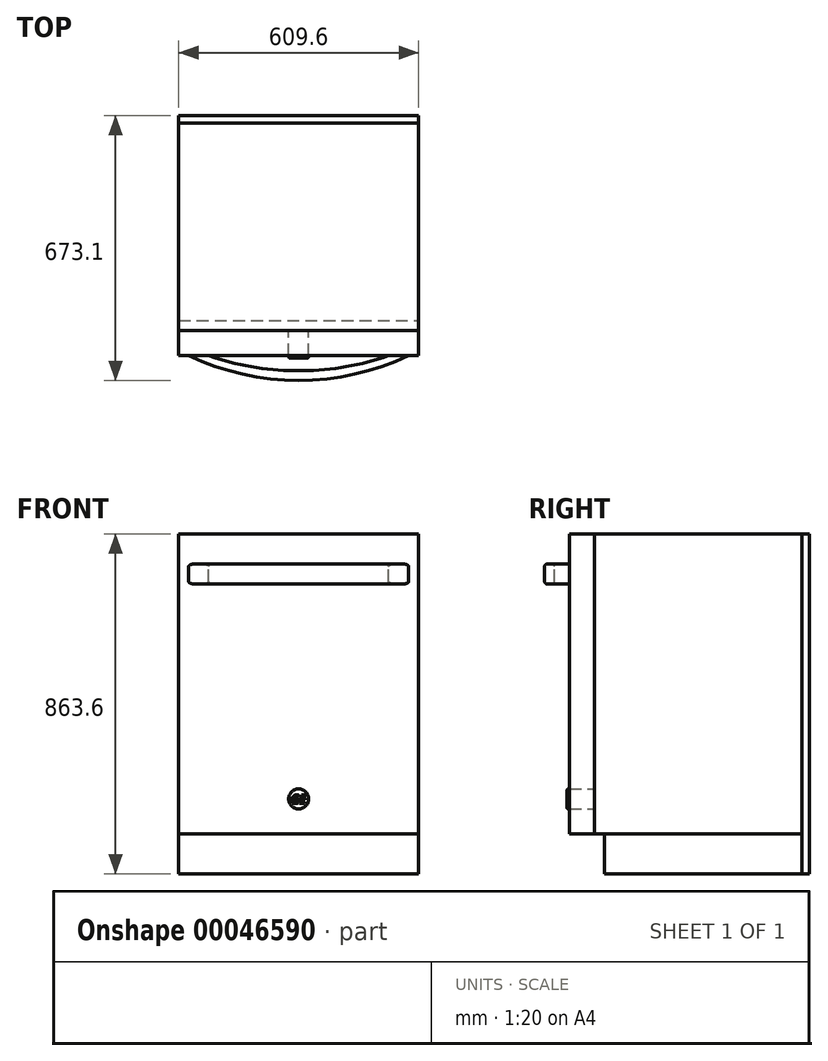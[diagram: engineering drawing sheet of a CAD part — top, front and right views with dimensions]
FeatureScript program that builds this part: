
annotation { "Feature Type Name" : "Feature", "Feature Type Description" : "" }
export const myFeature = defineFeature(function(context is Context, id is Id, definition is map)
    precondition{}
    {
        {
            var Q0;
            Q0=qCreatedBy(makeId("Front.planeOp"),FACE);
            var sketch = newSketch(context, id + "F0", { "sketchPlane" : qUnion([Q0])});
            skLineSegment(sketch, "E0.bottom", {"start": v(-304.8, 431.8) * mm, "end": v(304.8, 431.8) * mm});
            skLineSegment(sketch, "E0.top", {"start": v(-304.8, -431.8) * mm, "end": v(304.8, -431.8) * mm});
            skLineSegment(sketch, "E0.left", {"start": v(-304.8, 431.8) * mm, "end": v(-304.8, -431.8) * mm});
            skLineSegment(sketch, "E0.right", {"start": v(304.8, 431.8) * mm, "end": v(304.8, -431.8) * mm});
            skLineSegment(sketch, "E1", {"start": v(-304.8, 431.8) * mm, "end": v(304.8, -431.8) * mm, "construction": true});
            skLineSegment(sketch, "E2.bottom", {"start": v(-304.8, -330.2) * mm, "end": v(304.8, -330.2) * mm});
            skLineSegment(sketch, "E2.left", {"start": v(-304.8, -330.2) * mm, "end": v(-304.8, 431.8) * mm});
            skLineSegment(sketch, "E2.right", {"start": v(304.8, -330.2) * mm, "end": v(304.8, 431.8) * mm});
            skLineSegment(sketch, "E3", {"start": v(0, 0) * mm, "end": v(0, -330.2) * mm, "construction": true});
            skCircle(sketch, "E4", {"center": v(0, -241.3) * mm, "radius": 25.4 * mm});
            skLineSegment(sketch, "E5.bottom", {"start": v(-279.4, 355.6) * mm, "end": v(279.4, 355.6) * mm});
            skLineSegment(sketch, "E5.top", {"start": v(-279.4, 304.8) * mm, "end": v(279.4, 304.8) * mm});
            skLineSegment(sketch, "E5.left", {"start": v(-279.4, 355.6) * mm, "end": v(-279.4, 304.8) * mm});
            skLineSegment(sketch, "E5.right", {"start": v(279.4, 355.6) * mm, "end": v(279.4, 304.8) * mm});
            skLineSegment(sketch, "E6", {"start": v(0, 431.8) * mm, "end": v(0, 304.8) * mm, "construction": true});
            skSolve(sketch);
        }
        {
            var Q0;
            Q0=makeQuery(id+"F0.imprint","IMPRINT",FACE,{"disambiguationData":[TD([[makeQuery(id+"F0.imprint","IMPRINT",EDGE,{"derivedFrom":sQuery(id+"F0.wireOp",EDGE,"E2.bottom")}),1.0]])]});
            var Q1;
            Q1=makeQuery(id+"F0.imprint","IMPRINT",FACE,{"disambiguationData":[TD([[makeQuery(id+"F0.imprint","IMPRINT",EDGE,{"derivedFrom":sQuery(id+"F0.wireOp",EDGE,"E5.bottom")}),-1.0]])]});
            var Q2;
            Q2=makeQuery(id+"F0.imprint","IMPRINT",FACE,{"disambiguationData":[TD([[makeQuery(id+"F0.imprint","IMPRINT",EDGE,{"derivedFrom":sQuery(id+"F0.wireOp",EDGE,"E4")}),1.0]])]});
            var Q3;
            Q3=sQuery(id+"F0.wireOp",EDGE,"E2.right");
            var Q4;
            Q4=sQuery(id+"F0.wireOp",EDGE,"E0.bottom");
            var Q5;
            Q5=sQuery(id+"F0.wireOp",EDGE,"E2.left");
            var Q6;
            Q6=sQuery(id+"F0.wireOp",EDGE,"E2.bottom");
            extrude(context, id + "F1", {"entities" : qUnion([Q0, Q1, Q2]), "surfaceEntities" : qUnion([Q3, Q4, Q5, Q6]), "depth" : 63.5 * mm});
        }
        {
            var Q0;
            Q0=makeQuery(id+"F0.imprint","IMPRINT",FACE,{"disambiguationData":[TD([[makeQuery(id+"F0.imprint","IMPRINT",EDGE,{"derivedFrom":sQuery(id+"F0.wireOp",EDGE,"E0.top")}),1.0]])]});
            extrude(context, id + "F2", {"entities" : qUnion([Q0]), "oppositeDirection" : true, "depth" : 527.05 * mm});
        }
        {
            var Q0;
            Q0=makeQuery(id+"F0.imprint","IMPRINT",FACE,{"disambiguationData":[TD([[makeQuery(id+"F0.imprint","IMPRINT",EDGE,{"derivedFrom":sQuery(id+"F0.wireOp",EDGE,"E5.bottom")}),-1.0]])]});
            extrude(context, id + "F3", {"entities" : qUnion([Q0]), "operationType" : NewBodyOperationType.ADD, "depth" : 127 * mm});
        }
        {
            var Q0;
            Q0=makeQuery(id+"F3.opExtrude","SWEPT_FACE",FACE,{"disambiguationData":[OSD([sQuery(id+"F0.wireOp",EDGE,"E5.bottom")])]});
            var sketch = newSketch(context, id + "F4", { "sketchPlane" : qUnion([Q0])});
            skLineSegment(sketch, "E7.bottom", {"start": v(-228.6, -63.5) * mm, "end": v(228.6, -63.5) * mm});
            skLineSegment(sketch, "E7.top", {"start": v(-228.6, -101.6) * mm, "end": v(228.6, -101.6) * mm});
            skLineSegment(sketch, "E7.left", {"start": v(-228.6, -63.5) * mm, "end": v(-228.6, -101.6) * mm});
            skLineSegment(sketch, "E7.right", {"start": v(228.6, -63.5) * mm, "end": v(228.6, -101.6) * mm});
            skSolve(sketch);
        }
        {
            var Q0;
            Q0 = qSketchRegion(id + "F4", true);
            extrude(context, id + "F5", {"entities" : qUnion([Q0]), "operationType" : NewBodyOperationType.REMOVE, "endBound" : BoundingType.THROUGH_ALL, "oppositeDirection" : true, "depth" : 25.4 * mm});
        }
        {
            var Q0;
            Q0=makeQuery(id+"F5.boolean.opBoolean","COPY",EDGE,{"derivedFrom":makeQuery(id+"F5.opExtrude","SWEPT_EDGE",EDGE,{"disambiguationData":[OSD([sQuery(id+"F4.wireOp",EDGE,"E7.top"),sQuery(id+"F4.wireOp",EDGE,"E7.right")])]})});
            var Q1;
            Q1=makeQuery(id+"F5.boolean.opBoolean","COPY",EDGE,{"derivedFrom":makeQuery(id+"F5.opExtrude","SWEPT_EDGE",EDGE,{"disambiguationData":[OSD([sQuery(id+"F4.wireOp",EDGE,"E7.top"),sQuery(id+"F4.wireOp",EDGE,"E7.left")])]})});
            var Q2;
            Q2=makeQuery(id+"F3.opExtrude","CAP_EDGE",EDGE,{"disambiguationData":[OSD([sQuery(id+"F0.wireOp",EDGE,"E5.left")])],"isStart":false});
            var Q3;
            Q3=makeQuery(id+"F3.opExtrude","CAP_EDGE",EDGE,{"disambiguationData":[OSD([sQuery(id+"F0.wireOp",EDGE,"E5.right")])],"isStart":false});
            fillet(context, id + "F6", {"entities" : qUnion([Q0, Q1, Q2, Q3]), "radius" : 646.43 * mm, "tangentPropagation" : true, "allowEdgeOverflow" : false});
        }
        {
            var Q0;
            Q0=makeQuery(id+"F6.opFillet","BLEND_EDGE",EDGE,{"blendedFrom":[makeQuery(id+"F3.opExtrude","CAP_EDGE",EDGE,{"disambiguationData":[OSD([sQuery(id+"F0.wireOp",EDGE,"E5.left")])],"isStart":false}),makeQuery(id+"F3.opExtrude","SWEPT_FACE",FACE,{"disambiguationData":[OSD([sQuery(id+"F0.wireOp",EDGE,"E5.bottom")])]})],"blendedInto":[makeQuery(id+"F3.opExtrude","SWEPT_FACE",FACE,{"disambiguationData":[OSD([sQuery(id+"F0.wireOp",EDGE,"E5.bottom")])]})]});
            var Q1;
            Q1=makeQuery(id+"F6.opFillet","BLEND_EDGE",EDGE,{"blendedFrom":[makeQuery(id+"F5.boolean.opBoolean","COPY",EDGE,{"derivedFrom":makeQuery(id+"F5.opExtrude","SWEPT_EDGE",EDGE,{"disambiguationData":[OSD([sQuery(id+"F4.wireOp",EDGE,"E7.top"),sQuery(id+"F4.wireOp",EDGE,"E7.right")])]})}),makeQuery(id+"F3.opExtrude","SWEPT_FACE",FACE,{"disambiguationData":[OSD([sQuery(id+"F0.wireOp",EDGE,"E5.bottom")])]})],"blendedInto":[makeQuery(id+"F3.opExtrude","SWEPT_FACE",FACE,{"disambiguationData":[OSD([sQuery(id+"F0.wireOp",EDGE,"E5.bottom")])]})]});
            var Q2;
            Q2=makeQuery(id+"F6.opFillet","BLEND_EDGE",EDGE,{"blendedFrom":[makeQuery(id+"F5.boolean.opBoolean","COPY",EDGE,{"derivedFrom":makeQuery(id+"F5.opExtrude","SWEPT_EDGE",EDGE,{"disambiguationData":[OSD([sQuery(id+"F4.wireOp",EDGE,"E7.top"),sQuery(id+"F4.wireOp",EDGE,"E7.left")])]})}),makeQuery(id+"F3.opExtrude","SWEPT_FACE",FACE,{"disambiguationData":[OSD([sQuery(id+"F0.wireOp",EDGE,"E5.bottom")])]})],"blendedInto":[makeQuery(id+"F3.opExtrude","SWEPT_FACE",FACE,{"disambiguationData":[OSD([sQuery(id+"F0.wireOp",EDGE,"E5.bottom")])]})]});
            var Q3;
            Q3=makeQuery(id+"F5.boolean.opBoolean","COPY",EDGE,{"derivedFrom":makeQuery(id+"F5.opExtrude","CAP_EDGE",EDGE,{"disambiguationData":[OSD([sQuery(id+"F4.wireOp",EDGE,"E7.top")])],"isStart":true})});
            var Q4;
            Q4=makeQuery(id+"F6.opFillet","BLEND_EDGE",EDGE,{"blendedFrom":[makeQuery(id+"F3.opExtrude","CAP_EDGE",EDGE,{"disambiguationData":[OSD([sQuery(id+"F0.wireOp",EDGE,"E5.right")])],"isStart":false}),makeQuery(id+"F3.opExtrude","SWEPT_FACE",FACE,{"disambiguationData":[OSD([sQuery(id+"F0.wireOp",EDGE,"E5.bottom")])]})],"blendedInto":[makeQuery(id+"F3.opExtrude","SWEPT_FACE",FACE,{"disambiguationData":[OSD([sQuery(id+"F0.wireOp",EDGE,"E5.bottom")])]})]});
            var Q5;
            Q5=makeQuery(id+"F6.opFillet","BLEND_EDGE",EDGE,{"blendedFrom":[makeQuery(id+"F3.opExtrude","CAP_EDGE",EDGE,{"disambiguationData":[OSD([sQuery(id+"F0.wireOp",EDGE,"E5.right")])],"isStart":false}),makeQuery(id+"F3.opExtrude","SWEPT_FACE",FACE,{"disambiguationData":[OSD([sQuery(id+"F0.wireOp",EDGE,"E5.top")])]})],"blendedInto":[makeQuery(id+"F3.opExtrude","SWEPT_FACE",FACE,{"disambiguationData":[OSD([sQuery(id+"F0.wireOp",EDGE,"E5.top")])]})]});
            var Q6;
            Q6=makeQuery(id+"F6.opFillet","BLEND_EDGE",EDGE,{"blendedFrom":[makeQuery(id+"F3.opExtrude","CAP_EDGE",EDGE,{"disambiguationData":[OSD([sQuery(id+"F0.wireOp",EDGE,"E5.left")])],"isStart":false}),makeQuery(id+"F3.opExtrude","SWEPT_FACE",FACE,{"disambiguationData":[OSD([sQuery(id+"F0.wireOp",EDGE,"E5.top")])]})],"blendedInto":[makeQuery(id+"F3.opExtrude","SWEPT_FACE",FACE,{"disambiguationData":[OSD([sQuery(id+"F0.wireOp",EDGE,"E5.top")])]})]});
            var Q7;
            Q7=makeQuery(id+"F6.opFillet","BLEND_EDGE",EDGE,{"blendedFrom":[makeQuery(id+"F5.boolean.opBoolean","COPY",EDGE,{"derivedFrom":makeQuery(id+"F5.opExtrude","SWEPT_EDGE",EDGE,{"disambiguationData":[OSD([sQuery(id+"F4.wireOp",EDGE,"E7.top"),sQuery(id+"F4.wireOp",EDGE,"E7.left")])]})}),makeQuery(id+"F3.opExtrude","SWEPT_FACE",FACE,{"disambiguationData":[OSD([sQuery(id+"F0.wireOp",EDGE,"E5.top")])]})],"blendedInto":[makeQuery(id+"F3.opExtrude","SWEPT_FACE",FACE,{"disambiguationData":[OSD([sQuery(id+"F0.wireOp",EDGE,"E5.top")])]})]});
            var Q8;
            Q8=makeQuery(id+"F6.opFillet","BLEND_EDGE",EDGE,{"blendedFrom":[makeQuery(id+"F5.boolean.opBoolean","COPY",EDGE,{"derivedFrom":makeQuery(id+"F5.opExtrude","SWEPT_EDGE",EDGE,{"disambiguationData":[OSD([sQuery(id+"F4.wireOp",EDGE,"E7.top"),sQuery(id+"F4.wireOp",EDGE,"E7.right")])]})}),makeQuery(id+"F3.opExtrude","SWEPT_FACE",FACE,{"disambiguationData":[OSD([sQuery(id+"F0.wireOp",EDGE,"E5.top")])]})],"blendedInto":[makeQuery(id+"F3.opExtrude","SWEPT_FACE",FACE,{"disambiguationData":[OSD([sQuery(id+"F0.wireOp",EDGE,"E5.top")])]})]});
            var Q9;
            Q9=makeQuery(id+"F5.boolean.opBoolean","INTERSECT",EDGE,{"derivedFrom":[makeQuery(id+"F3.opExtrude","SWEPT_FACE",FACE,{"disambiguationData":[OSD([sQuery(id+"F0.wireOp",EDGE,"E5.top")])]}),makeQuery(id+"F5.opExtrude","SWEPT_FACE",FACE,{"disambiguationData":[OSD([sQuery(id+"F4.wireOp",EDGE,"E7.top")])]})]});
            fillet(context, id + "F7", {"entities" : qUnion([Q0, Q1, Q2, Q3, Q4, Q5, Q6, Q7, Q8, Q9]), "radius" : 6.35 * mm, "tangentPropagation" : true, "allowEdgeOverflow" : false});
        }
        {
            var Q0;
            Q0=makeQuery(id+"F1.opExtrude","CAP_FACE",FACE,{"disambiguationData":[OSD([sQuery(id+"F0.wireOp",EDGE,"E2.bottom"),sQuery(id+"F0.wireOp",EDGE,"E0.bottom"),sQuery(id+"F0.wireOp",EDGE,"E2.left"),sQuery(id+"F0.wireOp",EDGE,"E2.right")])],"isStart":true});
            var Q1;
            Q1=makeQuery(id+"F2.opExtrude","CAP_FACE",FACE,{"disambiguationData":[OSD([sQuery(id+"F0.wireOp",EDGE,"E0.top"),sQuery(id+"F0.wireOp",EDGE,"E0.left"),sQuery(id+"F0.wireOp",EDGE,"E0.right"),sQuery(id+"F0.wireOp",EDGE,"E2.bottom")])],"isStart":false});
            extrude(context, id + "F8", {"entities" : qUnion([Q0]), "endBound" : BoundingType.UP_TO_SURFACE, "endBoundEntityFace" : qUnion([Q1]), "depth" : 25.4 * mm});
        }
        {
            var Q0;
            Q0=makeQuery(id+"F1.opExtrude","SWEPT_EDGE",EDGE,{"disambiguationData":[OSD([sQuery(id+"F0.wireOp",EDGE,"E0.left"),sQuery(id+"F0.wireOp",EDGE,"E2.bottom"),sQuery(id+"F0.wireOp",EDGE,"E2.left")])]});
            var Q1;
            Q1=makeQuery(id+"F1.opExtrude","SWEPT_EDGE",EDGE,{"disambiguationData":[OSD([sQuery(id+"F0.wireOp",EDGE,"E0.right"),sQuery(id+"F0.wireOp",EDGE,"E2.bottom"),sQuery(id+"F0.wireOp",EDGE,"E2.right")])]});
            fillet(context, id + "F9", {"entities" : qUnion([Q0, Q1]), "radius" : 6.35 * mm, "tangentPropagation" : true, "allowEdgeOverflow" : false});
        }
        {
            var Q0;
            Q0=makeQuery(id+"F0.imprint","IMPRINT",FACE,{"disambiguationData":[TD([[makeQuery(id+"F0.imprint","IMPRINT",EDGE,{"derivedFrom":sQuery(id+"F0.wireOp",EDGE,"E4")}),1.0]])]});
            var Q1;
            Q1=sQuery(id+"F0.wireOp",EDGE,"E4");
            extrude(context, id + "F10", {"entities" : qUnion([Q0]), "surfaceEntities" : qUnion([Q1]), "depth" : 69.85 * mm});
        }
        {
            var Q0;
            Q0=makeQuery(id+"F10.opExtrude","CAP_EDGE",EDGE,{"disambiguationData":[OSD([sQuery(id+"F0.wireOp",EDGE,"E4")])],"isStart":false});
            fillet(context, id + "F11", {"entities" : qUnion([Q0]), "radius" : 3.17 * mm, "tangentPropagation" : true, "allowEdgeOverflow" : false});
        }
        {
            var Q0;
            Q0=makeQuery(id+"F10.opExtrude","CAP_FACE",FACE,{"disambiguationData":[OSD([sQuery(id+"F0.wireOp",EDGE,"E4")])],"isStart":false});
            var sketch = newSketch(context, id + "F12", { "sketchPlane" : qUnion([Q0])});
            skText(sketch, "E8", { "text": "GE", "fontName": "OpenSans-BoldItalic.ttf"});
            const initialGuessF12  = {"E8": [-0.0191, -0.25284, 1, 0, 0.02166]};
            skSetInitialGuess(sketch, initialGuessF12);
            skSolve(sketch);
        }
        {
            var Q0;
            Q0 = qSketchRegion(id + "F12", true);
            extrude(context, id + "F13", {"entities" : qUnion([Q0]), "operationType" : NewBodyOperationType.REMOVE, "oppositeDirection" : true, "depth" : 3.17 * mm});
        }
        {
            var Q0;
            Q0=makeQuery(id+"F2.opExtrude","CAP_FACE",FACE,{"disambiguationData":[OSD([sQuery(id+"F0.wireOp",EDGE,"E0.top"),sQuery(id+"F0.wireOp",EDGE,"E0.left"),sQuery(id+"F0.wireOp",EDGE,"E0.right"),sQuery(id+"F0.wireOp",EDGE,"E2.bottom")])],"isStart":true});
            extrude(context, id + "F14", {"entities" : qUnion([Q0]), "operationType" : NewBodyOperationType.REMOVE, "oppositeDirection" : true, "depth" : 25.4 * mm});
        }
        {
            var Q0;
            Q0=makeQuery(id+"F8.opExtrude","CAP_FACE",FACE,{"disambiguationData":[OSD([sQuery(id+"F0.wireOp",EDGE,"E2.bottom"),sQuery(id+"F0.wireOp",EDGE,"E0.bottom"),sQuery(id+"F0.wireOp",EDGE,"E2.left"),sQuery(id+"F0.wireOp",EDGE,"E2.right")])],"isStart":false});
            var sketch = newSketch(context, id + "F15", { "sketchPlane" : qUnion([Q0])});
            skLineSegment(sketch, "E9.bottom", {"start": v(304.8, 431.8) * mm, "end": v(-304.8, 431.8) * mm});
            skLineSegment(sketch, "E9.top", {"start": v(304.8, -431.8) * mm, "end": v(-304.8, -431.8) * mm});
            skLineSegment(sketch, "E9.left", {"start": v(304.8, 431.8) * mm, "end": v(304.8, -431.8) * mm});
            skLineSegment(sketch, "E9.right", {"start": v(-304.8, 431.8) * mm, "end": v(-304.8, -431.8) * mm});
            skSolve(sketch);
        }
        {
            var Q0;
            Q0 = qSketchRegion(id + "F15", true);
            extrude(context, id + "F16", {"entities" : qUnion([Q0]), "depth" : 19.05 * mm});
        }
    });
